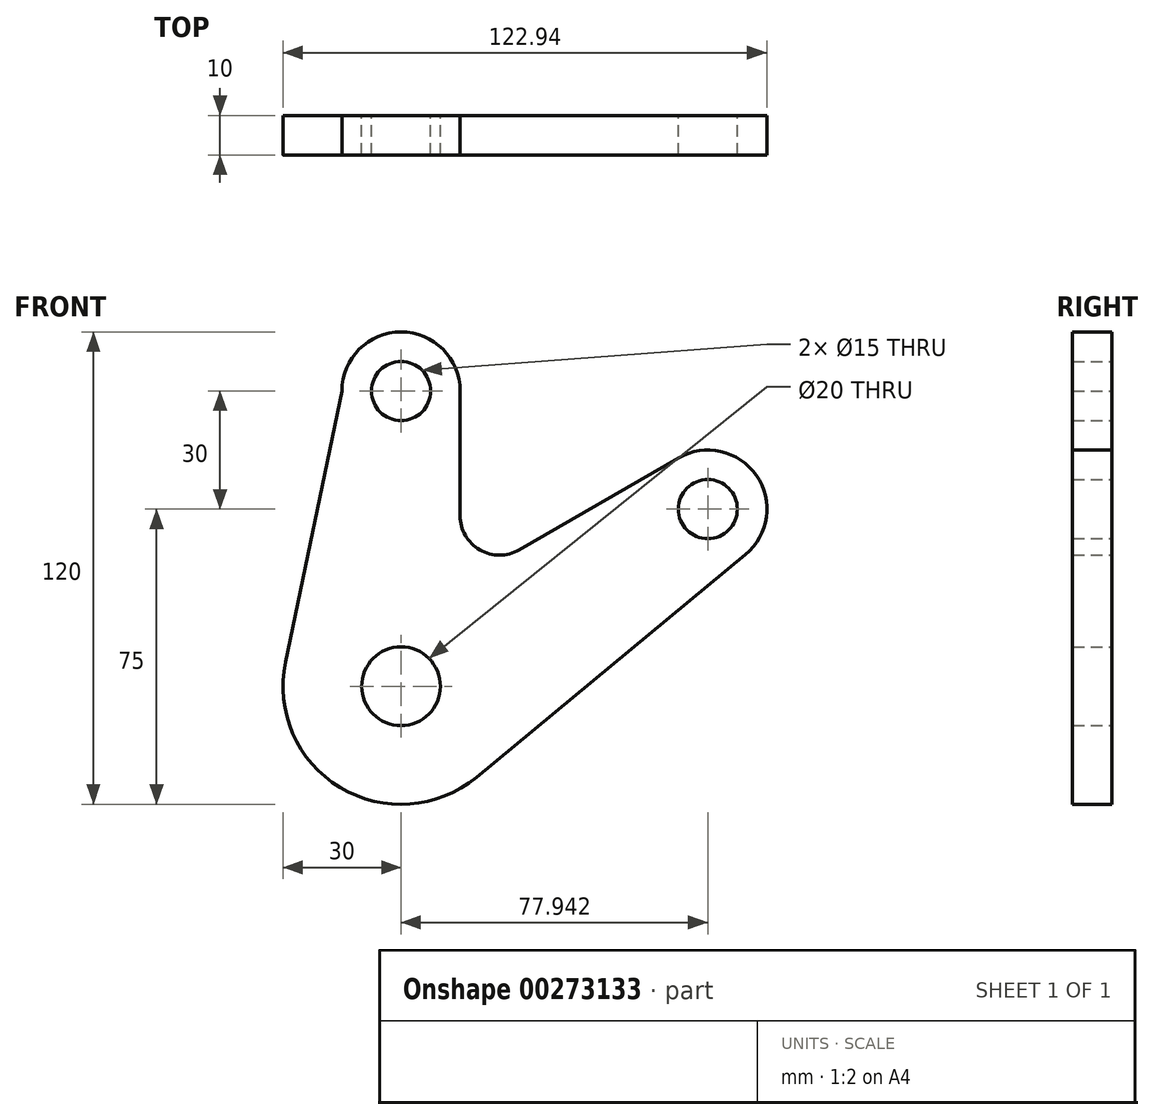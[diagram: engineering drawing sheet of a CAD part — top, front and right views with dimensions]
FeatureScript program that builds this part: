
annotation { "Feature Type Name" : "Feature", "Feature Type Description" : "" }
export const myFeature = defineFeature(function(context is Context, id is Id, definition is map)
    precondition{}
    {
        {
            var Q0;
            Q0=qCreatedBy(makeId("Front.planeOp"),FACE);
            var sketch = newSketch(context, id + "F0", { "sketchPlane" : qUnion([Q0])});
            skCircle(sketch, "E0", {"center": v(0, 0) * mm, "radius": 10 * mm});
            skLineSegment(sketch, "E1", {"start": v(0, 0) * mm, "end": v(0, 75) * mm, "construction": true});
            skCircle(sketch, "E2", {"center": v(0, 75) * mm, "radius": 7.5 * mm});
            skLineSegment(sketch, "E3", {"start": v(0, 0) * mm, "end": v(77.94, 45) * mm, "construction": true});
            skCircle(sketch, "E4", {"center": v(77.94, 45) * mm, "radius": 7.5 * mm});
            skArc(sketch, "E5", {"start": v(-29.37, 6.13) * mm, "mid": v(-15.5, -25.69) * mm, "end": v(19.12, -23.12) * mm});
            skArc(sketch, "E6", {"start": v(-15, 75) * mm, "mid": v(0, 90) * mm, "end": v(15, 75) * mm});
            skArc(sketch, "E7", {"start": v(70.44, 58) * mm, "mid": v(90.26, 53.56) * mm, "end": v(87.5, 33.44) * mm});
            skLineSegment(sketch, "E8", {"start": v(-29.37, 6.13) * mm, "end": v(-15, 75) * mm});
            skLineSegment(sketch, "E9", {"start": v(19.12, -23.12) * mm, "end": v(87.5, 33.44) * mm});
            skLineSegment(sketch, "E10", {"start": v(70.44, 58) * mm, "end": v(30, 34.64) * mm});
            skLineSegment(sketch, "E11", {"start": v(15, 75) * mm, "end": v(15, 43.3) * mm});
            skArc(sketch, "E12", {"start": v(15, 43.3) * mm, "mid": v(20, 34.64) * mm, "end": v(30, 34.64) * mm});
            skSolve(sketch);
        }
        {
            var Q0;
            Q0=makeQuery(id+"F0.imprint","IMPRINT",FACE,{"disambiguationData":[TD([[makeQuery(id+"F0.imprint","IMPRINT",EDGE,{"derivedFrom":sQuery(id+"F0.wireOp",EDGE,"E0")}),-1.0]])]});
            extrude(context, id + "F1", {"entities" : qUnion([Q0]), "depth" : 10 * mm});
        }
    });
